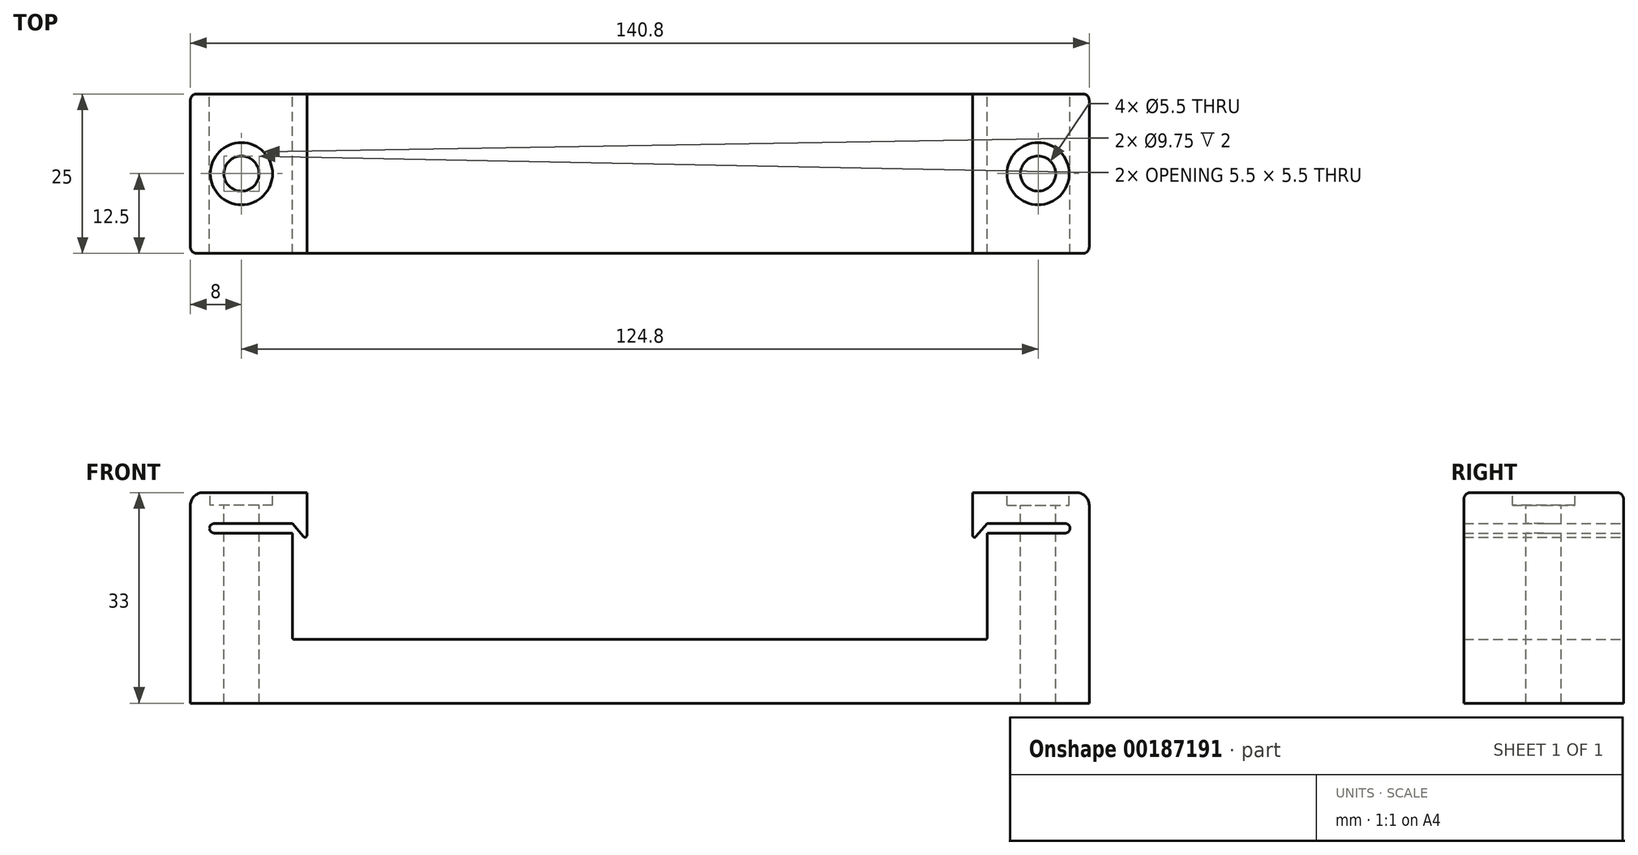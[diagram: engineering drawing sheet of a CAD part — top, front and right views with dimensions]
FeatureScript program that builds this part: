
annotation { "Feature Type Name" : "Feature", "Feature Type Description" : "" }
export const myFeature = defineFeature(function(context is Context, id is Id, definition is map)
    precondition{}
    {
        {
            var Q0;
            Q0=qCreatedBy(makeId("Front.planeOp"),FACE);
            var sketch = newSketch(context, id + "F0", { "sketchPlane" : qUnion([Q0])});
            skLineSegment(sketch, "E0.bottom", {"start": v(0, 0) * mm, "end": v(70.4, 0) * mm});
            skLineSegment(sketch, "E0.top", {"start": v(0, 33) * mm, "end": v(18.25, 33) * mm});
            skLineSegment(sketch, "E0.left", {"start": v(0, 0) * mm, "end": v(0, 33) * mm});
            skLineSegment(sketch, "E1.top", {"start": v(16.2, 10) * mm, "end": v(70.4, 10) * mm});
            skLineSegment(sketch, "E1.left", {"start": v(16, 26.66) * mm, "end": v(16, 10.2) * mm});
            skLineSegment(sketch, "E2", {"start": v(70.4, 37.27) * mm, "end": v(70.4, -5.43) * mm, "construction": true});
            skLineSegment(sketch, "E3", {"start": v(18.25, 33) * mm, "end": v(18.25, 26.3) * mm});
            skLineSegment(sketch, "E4", {"start": v(17.72, 26.1) * mm, "end": v(16, 28.16) * mm});
            skPoint(sketch, "E5.visualSharp", {"position": v(18.25, 25.48) * mm});
            skArc(sketch, "E5.filletArc", {"start": v(17.72, 26.1) * mm, "mid": v(18.05, 26.02) * mm, "end": v(18.25, 26.3) * mm});
            skPoint(sketch, "E6.visualSharp", {"position": v(16, 10) * mm});
            skArc(sketch, "E6.filletArc", {"start": v(16, 10.2) * mm, "mid": v(16.06, 10.06) * mm, "end": v(16.2, 10) * mm});
            skLineSegment(sketch, "E7", {"start": v(70.4, 10) * mm, "end": v(70.4, 0) * mm});
            skLineSegment(sketch, "E8.bottom", {"start": v(16, 28.16) * mm, "end": v(3.75, 28.16) * mm});
            skLineSegment(sketch, "E8.top", {"start": v(16, 26.66) * mm, "end": v(3.75, 26.66) * mm});
            skArc(sketch, "E9", {"start": v(3.75, 28.16) * mm, "mid": v(3, 27.4) * mm, "end": v(3.75, 26.66) * mm});
            skSolve(sketch);
        }
        {
            var Q0;
            Q0=makeQuery(id+"F0.imprint","IMPRINT",FACE,{"disambiguationData":[TD([[makeQuery(id+"F0.imprint","IMPRINT",EDGE,{"derivedFrom":sQuery(id+"F0.wireOp",EDGE,"E0.bottom")}),1.0]])]});
            extrude(context, id + "F1", {"entities" : qUnion([Q0]), "endBound" : BoundingType.SYMMETRIC, "depth" : 25 * mm});
        }
        {
            var Q0;
            Q0=makeQuery(id+"F1.opExtrude","SWEPT_FACE",FACE,{"disambiguationData":[OSD([sQuery(id+"F0.wireOp",EDGE,"E7")])]});
            cPlane(context, id + "F2", {"entities" : qUnion([Q0]), "cplaneType" : CPlaneType.OFFSET, "offset" : 0 * mm, "width" : 150 * mm, "height" : 150 * mm});
        }
        {
            var Q0;
            Q0=makeQuery(id+"F1.opExtrude","SWEPT_FACE",FACE,{"disambiguationData":[OSD([sQuery(id+"F0.wireOp",EDGE,"E0.top")])]});
            var sketch = newSketch(context, id + "F3", { "sketchPlane" : qUnion([Q0])});
            skPoint(sketch, "E10", {"position": v(8, 0) * mm});
            skLineSegment(sketch, "E11", {"start": v(8, -12.5) * mm, "end": v(8, 12.5) * mm, "construction": true});
            skSolve(sketch);
        }
        {
            var Q0;
            Q0=sQuery(id+"F3.wireOp",VERTEX,"E10");
            var Q1;
            Q1=makeQuery(id+"F1.opExtrude","SWEPT_BODY",BODY,{"disambiguationData":[OSD([sQuery(id+"F0.wireOp",EDGE,"E0.bottom"),sQuery(id+"F0.wireOp",EDGE,"E0.top"),sQuery(id+"F0.wireOp",EDGE,"E0.left"),sQuery(id+"F0.wireOp",EDGE,"E1.top"),sQuery(id+"F0.wireOp",EDGE,"E1.left"),sQuery(id+"F0.wireOp",EDGE,"E3"),sQuery(id+"F0.wireOp",EDGE,"E4"),sQuery(id+"F0.wireOp",EDGE,"E5.filletArc"),sQuery(id+"F0.wireOp",EDGE,"E6.filletArc"),sQuery(id+"F0.wireOp",EDGE,"E7"),sQuery(id+"F0.wireOp",EDGE,"E8.bottom"),sQuery(id+"F0.wireOp",EDGE,"E8.top"),sQuery(id+"F0.wireOp",EDGE,"E9")])]});
            hole(context, id + "F4", {"style" : HoleStyle.C_BORE, "endStyle" : HoleEndStyle.THROUGH, "standardTappedOrClearance" : lookupTablePath({ "standard" : "ISO", "fit" : "Normal", "size" : "M5", "type" : "Clearance" }), "standardBlindInLast" : lookupTablePath({ "fit" : "Standard", "standard" : "ISO", "size" : "M5", "type" : "Clearance" }), "holeDiameter" : 5.5 * mm, "cBoreDiameter" : 9.75 * mm, "cBoreDepth" : 2 * mm, "locations" : qUnion([Q0]), "scope" : qUnion([Q1]), "isTappedThrough" : true});
        }
        {
            var Q0;
            Q0=makeQuery(id+"F1.opExtrude","SWEPT_EDGE",EDGE,{"disambiguationData":[OSD([sQuery(id+"F0.wireOp",EDGE,"E0.top"),sQuery(id+"F0.wireOp",EDGE,"E0.left")])]});
            fillet(context, id + "F5", {"entities" : qUnion([Q0]), "radius" : 2 * mm, "tangentPropagation" : true, "allowEdgeOverflow" : false});
        }
        {
            var Q0;
            Q0=makeQuery(id+"F1.opExtrude","CAP_EDGE",EDGE,{"disambiguationData":[OSD([sQuery(id+"F0.wireOp",EDGE,"E0.top")])],"isStart":false});
            var Q1;
            {var subQ0=sQuery(id+"F0.wireOp",EDGE,"E0.left");var subQ1=sQuery(id+"F0.wireOp",EDGE,"E0.top");Q1=makeQuery(id+"F5.opFillet","BLEND_EDGE",EDGE,{"blendedFrom":[makeQuery(id+"F1.opExtrude","SWEPT_EDGE",EDGE,{"disambiguationData":[OSD([subQ1,subQ0])]}),makeQuery(id+"F1.opExtrude","CAP_FACE",FACE,{"disambiguationData":[OSD([sQuery(id+"F0.wireOp",EDGE,"E0.bottom"),subQ1,subQ0,sQuery(id+"F0.wireOp",EDGE,"E1.top"),sQuery(id+"F0.wireOp",EDGE,"E1.left"),sQuery(id+"F0.wireOp",EDGE,"E3"),sQuery(id+"F0.wireOp",EDGE,"E4"),sQuery(id+"F0.wireOp",EDGE,"E5.filletArc"),sQuery(id+"F0.wireOp",EDGE,"E6.filletArc"),sQuery(id+"F0.wireOp",EDGE,"E7"),sQuery(id+"F0.wireOp",EDGE,"E8.bottom"),sQuery(id+"F0.wireOp",EDGE,"E8.top"),sQuery(id+"F0.wireOp",EDGE,"E9")])],"isStart":false})],"blendedInto":[makeQuery(id+"F1.opExtrude","CAP_FACE",FACE,{"disambiguationData":[OSD([sQuery(id+"F0.wireOp",EDGE,"E0.bottom"),subQ1,subQ0,sQuery(id+"F0.wireOp",EDGE,"E1.top"),sQuery(id+"F0.wireOp",EDGE,"E1.left"),sQuery(id+"F0.wireOp",EDGE,"E3"),sQuery(id+"F0.wireOp",EDGE,"E4"),sQuery(id+"F0.wireOp",EDGE,"E5.filletArc"),sQuery(id+"F0.wireOp",EDGE,"E6.filletArc"),sQuery(id+"F0.wireOp",EDGE,"E7"),sQuery(id+"F0.wireOp",EDGE,"E8.bottom"),sQuery(id+"F0.wireOp",EDGE,"E8.top"),sQuery(id+"F0.wireOp",EDGE,"E9")])],"isStart":false})]});}
            var Q2;
            Q2=makeQuery(id+"F1.opExtrude","CAP_EDGE",EDGE,{"disambiguationData":[OSD([sQuery(id+"F0.wireOp",EDGE,"E0.left")])],"isStart":false});
            var Q3;
            Q3=makeQuery(id+"F1.opExtrude","CAP_EDGE",EDGE,{"disambiguationData":[OSD([sQuery(id+"F0.wireOp",EDGE,"E0.top")])],"isStart":true});
            var Q4;
            {var subQ0=sQuery(id+"F0.wireOp",EDGE,"E0.left");var subQ1=sQuery(id+"F0.wireOp",EDGE,"E0.top");Q4=makeQuery(id+"F5.opFillet","BLEND_EDGE",EDGE,{"blendedFrom":[makeQuery(id+"F1.opExtrude","SWEPT_EDGE",EDGE,{"disambiguationData":[OSD([subQ1,subQ0])]}),makeQuery(id+"F1.opExtrude","CAP_FACE",FACE,{"disambiguationData":[OSD([sQuery(id+"F0.wireOp",EDGE,"E0.bottom"),subQ1,subQ0,sQuery(id+"F0.wireOp",EDGE,"E1.top"),sQuery(id+"F0.wireOp",EDGE,"E1.left"),sQuery(id+"F0.wireOp",EDGE,"E3"),sQuery(id+"F0.wireOp",EDGE,"E4"),sQuery(id+"F0.wireOp",EDGE,"E5.filletArc"),sQuery(id+"F0.wireOp",EDGE,"E6.filletArc"),sQuery(id+"F0.wireOp",EDGE,"E7"),sQuery(id+"F0.wireOp",EDGE,"E8.bottom"),sQuery(id+"F0.wireOp",EDGE,"E8.top"),sQuery(id+"F0.wireOp",EDGE,"E9")])],"isStart":true})],"blendedInto":[makeQuery(id+"F1.opExtrude","CAP_FACE",FACE,{"disambiguationData":[OSD([sQuery(id+"F0.wireOp",EDGE,"E0.bottom"),subQ1,subQ0,sQuery(id+"F0.wireOp",EDGE,"E1.top"),sQuery(id+"F0.wireOp",EDGE,"E1.left"),sQuery(id+"F0.wireOp",EDGE,"E3"),sQuery(id+"F0.wireOp",EDGE,"E4"),sQuery(id+"F0.wireOp",EDGE,"E5.filletArc"),sQuery(id+"F0.wireOp",EDGE,"E6.filletArc"),sQuery(id+"F0.wireOp",EDGE,"E7"),sQuery(id+"F0.wireOp",EDGE,"E8.bottom"),sQuery(id+"F0.wireOp",EDGE,"E8.top"),sQuery(id+"F0.wireOp",EDGE,"E9")])],"isStart":true})]});}
            var Q5;
            Q5=makeQuery(id+"F1.opExtrude","CAP_EDGE",EDGE,{"disambiguationData":[OSD([sQuery(id+"F0.wireOp",EDGE,"E0.left")])],"isStart":true});
            fillet(context, id + "F6", {"entities" : qUnion([Q0, Q1, Q2, Q3, Q4, Q5]), "radius" : 1 * mm, "tangentPropagation" : true, "allowEdgeOverflow" : false});
        }
        {
            var Q0;
            Q0=makeQuery(id+"F1.opExtrude","SWEPT_BODY",BODY,{"disambiguationData":[OSD([sQuery(id+"F0.wireOp",EDGE,"E0.bottom"),sQuery(id+"F0.wireOp",EDGE,"E0.top"),sQuery(id+"F0.wireOp",EDGE,"E0.left"),sQuery(id+"F0.wireOp",EDGE,"E1.top"),sQuery(id+"F0.wireOp",EDGE,"E1.left"),sQuery(id+"F0.wireOp",EDGE,"E3"),sQuery(id+"F0.wireOp",EDGE,"E4"),sQuery(id+"F0.wireOp",EDGE,"E5.filletArc"),sQuery(id+"F0.wireOp",EDGE,"E6.filletArc"),sQuery(id+"F0.wireOp",EDGE,"E7"),sQuery(id+"F0.wireOp",EDGE,"E8.bottom"),sQuery(id+"F0.wireOp",EDGE,"E8.top"),sQuery(id+"F0.wireOp",EDGE,"E9")])]});
            var Q1;
            Q1=qCreatedBy(id+"F2.planeOp",FACE);
            mirror(context, id + "F7", {"operationType" : NewBodyOperationType.ADD, "entities" : qUnion([Q0]), "mirrorPlane" : qUnion([Q1])});
        }
    });
